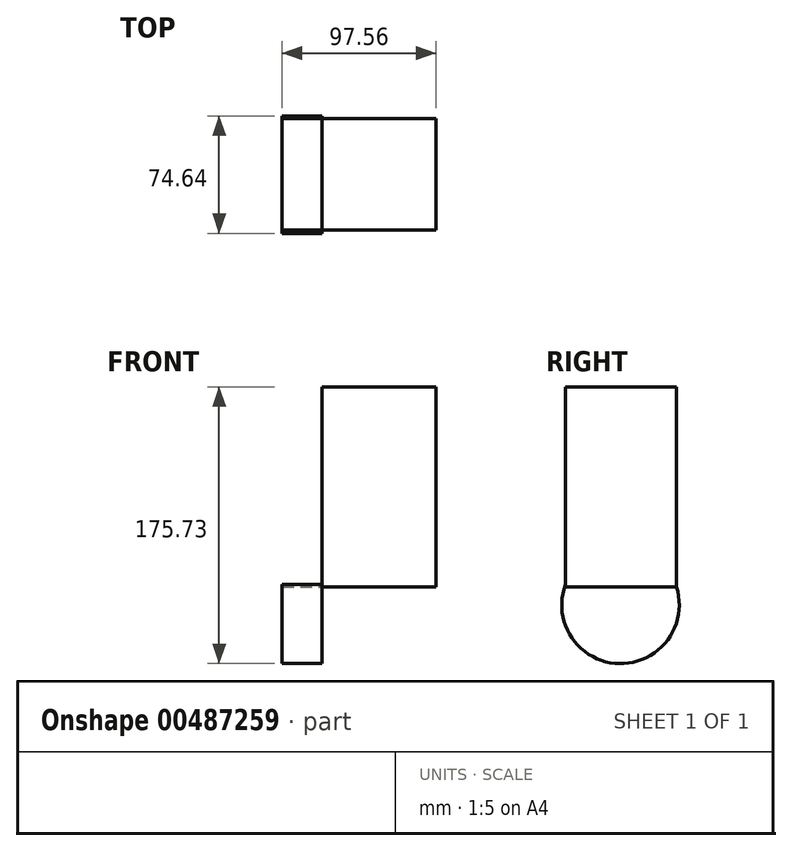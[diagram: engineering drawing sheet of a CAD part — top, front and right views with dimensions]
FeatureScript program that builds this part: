
annotation { "Feature Type Name" : "Feature", "Feature Type Description" : "" }
export const myFeature = defineFeature(function(context is Context, id is Id, definition is map)
    precondition{}
    {
        {
            var Q0;
            Q0=qCreatedBy(makeId("Top.planeOp"),FACE);
            var sketch = newSketch(context, id + "F0", { "sketchPlane" : qUnion([Q0])});
            skLineSegment(sketch, "E0.bottom", {"start": v(0, 0) * mm, "end": v(0, 0) * mm});
            skLineSegment(sketch, "E0.top", {"start": v(0, 0) * mm, "end": v(0, 0) * mm});
            skLineSegment(sketch, "E0.left", {"start": v(0, 0) * mm, "end": v(0, 0) * mm});
            skLineSegment(sketch, "E0.right", {"start": v(0, 0) * mm, "end": v(0, 0) * mm});
            skLineSegment(sketch, "E1.bottom", {"start": v(-3.13, -4.01) * mm, "end": v(-75.29, -4.01) * mm});
            skLineSegment(sketch, "E1.top", {"start": v(-3.13, -74.6) * mm, "end": v(-75.29, -74.6) * mm});
            skLineSegment(sketch, "E1.left", {"start": v(-3.13, -4.01) * mm, "end": v(-3.13, -74.6) * mm});
            skLineSegment(sketch, "E1.right", {"start": v(-75.29, -4.01) * mm, "end": v(-75.29, -74.6) * mm});
            skSolve(sketch);
        }
        {
            var Q0;
            Q0 = qSketchRegion(id + "F0", true);
            extrude(context, id + "F1", {"entities" : qUnion([Q0]), "depth" : 127 * mm});
        }
        {
            var Q0;
            Q0=makeQuery(id+"F1.opExtrude","SWEPT_FACE",FACE,{"disambiguationData":[OSD([sQuery(id+"F0.wireOp",EDGE,"E1.right")])]});
            var sketch = newSketch(context, id + "F2", { "sketchPlane" : qUnion([Q0])});
            skArc(sketch, "E2", {"start": v(4.01, 0) * mm, "mid": v(66.26, -37.47) * mm, "end": v(27.26, 23.83) * mm});
            skSolve(sketch);
        }
        {
            var Q0;
            {var subQ1=sQuery(id+"F0.wireOp",EDGE,"E1.right");var subQ2=makeQuery(id+"F1.opExtrude","CAP_EDGE",EDGE,{"disambiguationData":[OSD([subQ1])],"isStart":true});Q0=makeQuery(id+"F2.imprint","IMPRINT",FACE,{"disambiguationData":[TD([[makeQuery(id+"F2.imprint","IMPRINT",EDGE,{"derivedFrom":subQ2}),-1.0]])]});}
            extrude(context, id + "F3", {"entities" : qUnion([Q0]), "depth" : 25.4 * mm});
        }
    });
